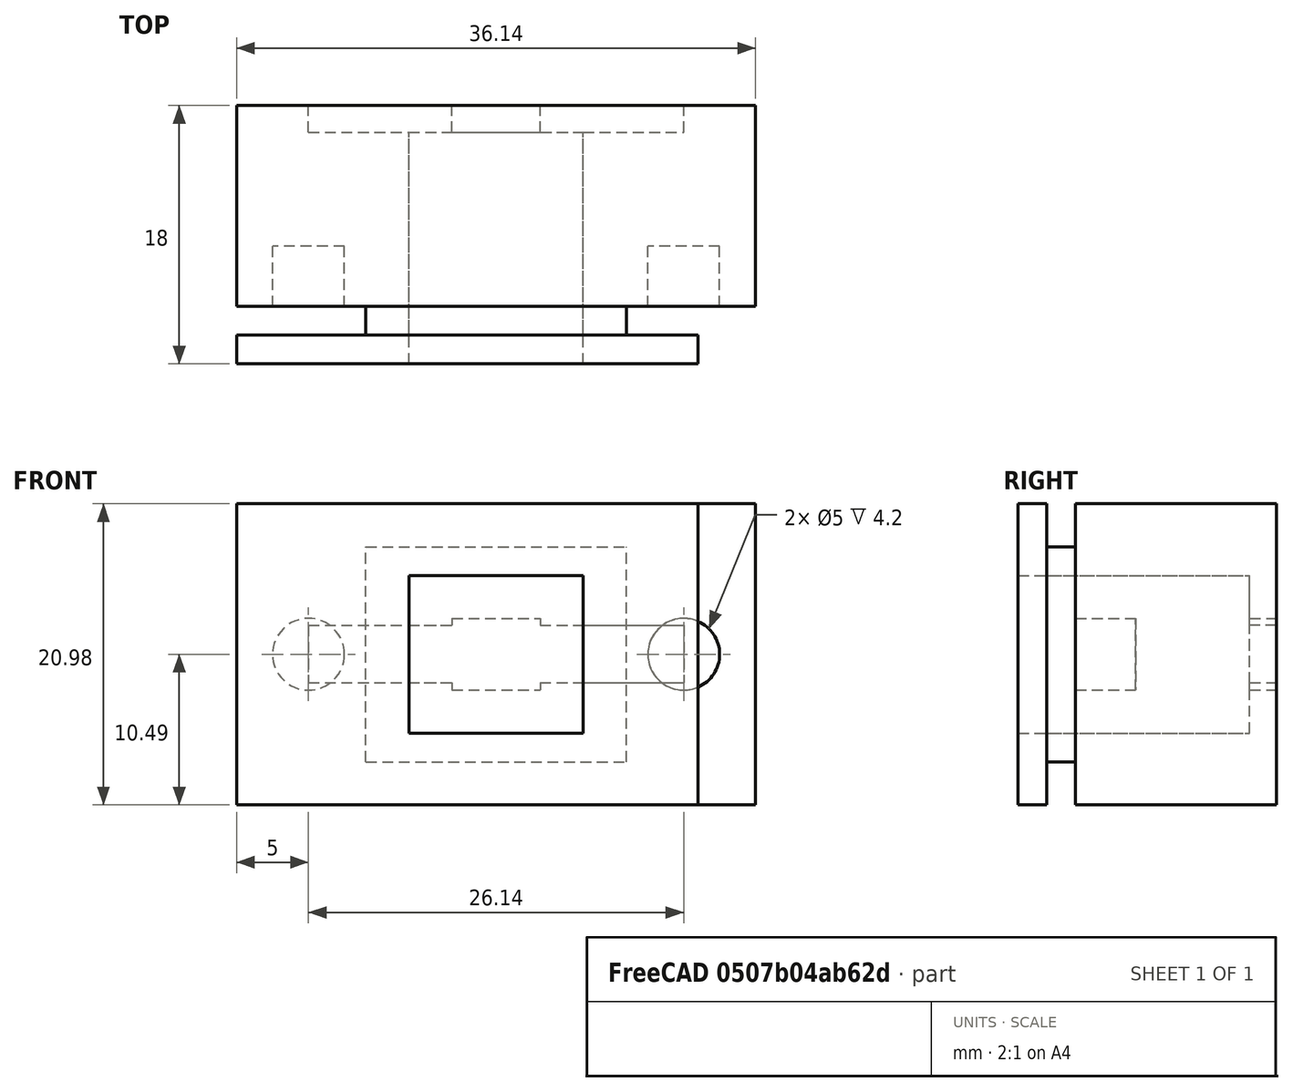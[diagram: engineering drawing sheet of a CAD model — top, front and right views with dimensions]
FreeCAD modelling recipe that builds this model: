
FCSTD DOCUMENT  (FreeCAD 0.18R16117 (Git))
Label: USB_B_Panelmount - Holes cut
License: All rights reserved
LicenseURL: http://en.wikipedia.org/wiki/All_rights_reserved
objects: Part::Box×8, Part::Cut×7, Part::Cylinder×2
note: 17 computed .brp shape members not serialized (recipe doc carries the construction recipe); baked Part::Feature solids carry a one-line shape summary decoded from their .brp

FEATURE [Part::Box] Box  label="USB"
  AttacherType = Attacher::AttachEngine3D
  Height = 10.98
  Length = 12.14
  Placement = pos=(12,0,5) rot=(0,0,1;0rad)
  Width = 16.14
FEATURE [Part::Box] Box001  label="Panel"
  AttacherType = Attacher::AttachEngine3D
  Height = 20.98
  Length = 32.14
  Width = 2
FEATURE [Part::Box] Box002  label="Cube001"
  AttacherType = Attacher::AttachEngine3D
  Height = 20.98
  Length = 36.14
  Placement = pos=(0,2,0) rot=(0,0,1;0rad)
  Width = 16
FEATURE [Part::Box] Box003  label="Cube002"
  AttacherType = Attacher::AttachEngine3D
  Height = 4.98
  Length = 6.14
  Placement = pos=(15,16.14,8) rot=(0,0,1;0rad)
  Width = 10
FEATURE [Part::Box] Box004  label="Cube003"
  AttacherType = Attacher::AttachEngine3D
  Height = 4
  Length = 26.14
  Placement = pos=(5,16.14,8.5) rot=(0,0,1;0rad)
  Width = 10
FEATURE [Part::Cylinder] Cylinder
  Angle = 360
  AttacherType = Attacher::AttachEngine3D
  Height = 4.2
  Placement = pos=(5,4,10.49) rot=(-1,0,0;1.5708rad)
  Radius = 2.5
FEATURE [Part::Box] Box005  label="Cube004"
  AttacherType = Attacher::AttachEngine3D
  Height = 10.98
  Length = 12.14
  Placement = pos=(12,0,5) rot=(0,0,1;0rad)
  Width = 16.14
FEATURE [Part::Cylinder] Cylinder001
  Angle = 360
  AttacherType = Attacher::AttachEngine3D
  Height = 4.2
  Placement = pos=(31.14,4,10.49) rot=(-1,0,0;1.5708rad)
  Radius = 2.5
FEATURE [Part::Cut] Cut
  Base = -> Box002
  Tool = -> Box005
FEATURE [Part::Cut] Cut001
  Base = -> Cut
  Tool = -> Box003
FEATURE [Part::Cut] Cut002
  Base = -> Cut001
  Tool = -> Box004
FEATURE [Part::Box] Box006  label="Cube"
  AttacherType = Attacher::AttachEngine3D
  Height = 20.98
  Length = 36.14
  Width = 4
FEATURE [Part::Box] Box007  label="Cube005"
  AttacherType = Attacher::AttachEngine3D
  Height = 14.98
  Length = 18.14
  Placement = pos=(9,0,3) rot=(0,0,1;0rad)
  Width = 4
FEATURE [Part::Cut] Cut003
  Base = -> Box006
  Tool = -> Box007
FEATURE [Part::Cut] Cut004
  Base = -> Cut002
  Tool = -> Cut003
FEATURE [Part::Cut] Cut005
  Base = -> Cut004
  Tool = -> Cylinder
FEATURE [Part::Cut] Cut006
  Base = -> Cut005
  Tool = -> Cylinder001
